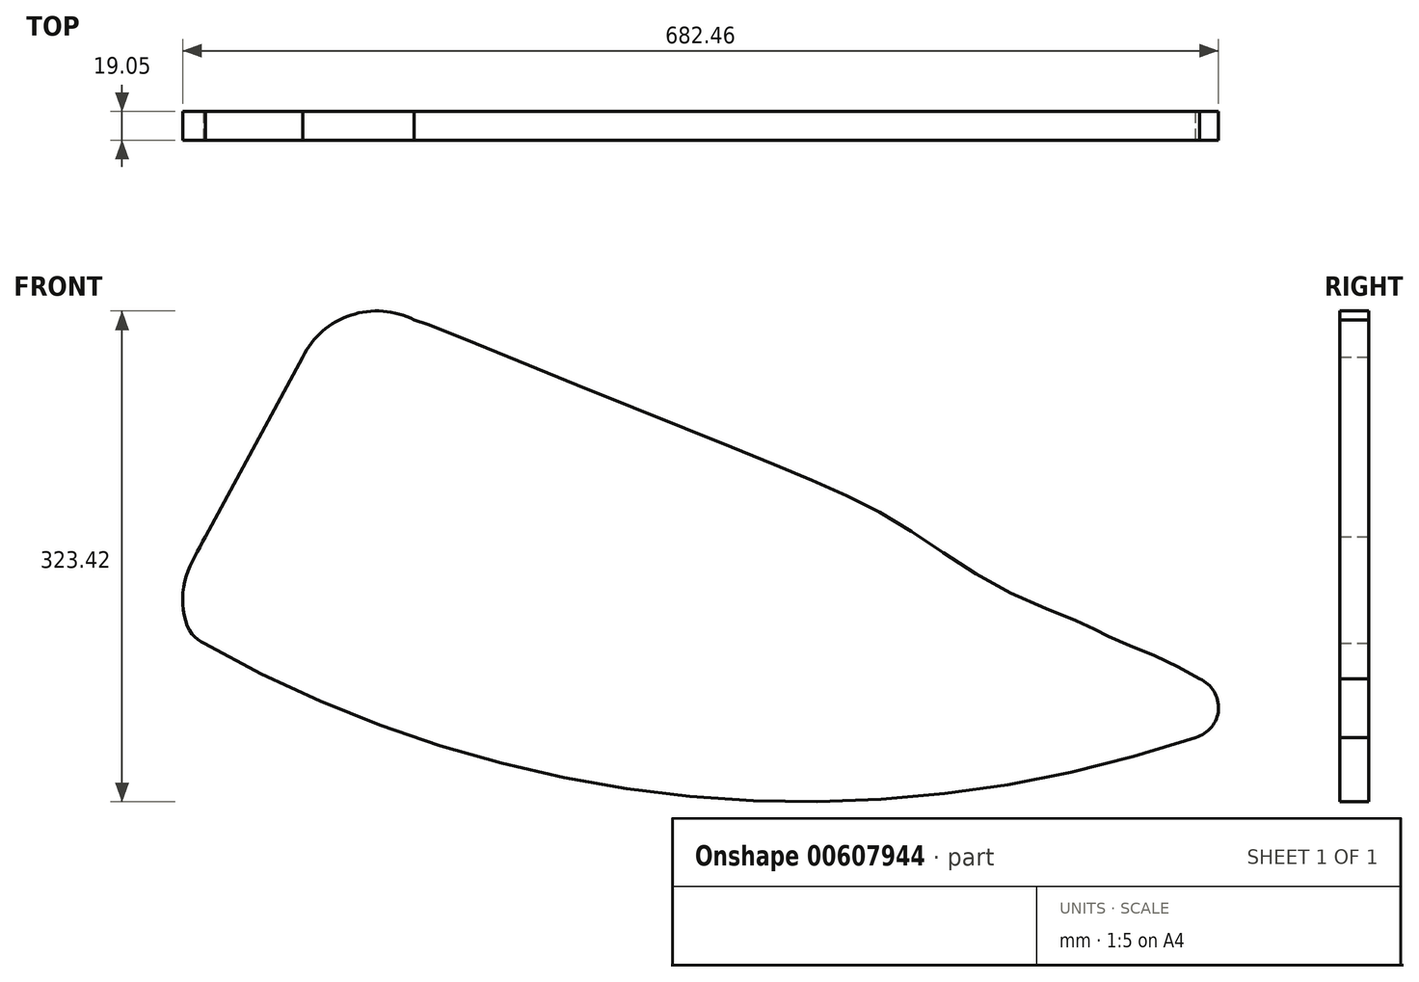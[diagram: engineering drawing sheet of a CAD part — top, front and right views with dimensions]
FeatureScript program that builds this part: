
annotation { "Feature Type Name" : "Feature", "Feature Type Description" : "" }
export const myFeature = defineFeature(function(context is Context, id is Id, definition is map)
    precondition{}
    {
        {
            var Q0;
            Q0=qCreatedBy(makeId("Front.planeOp"),FACE);
            var sketch = newSketch(context, id + "F0", { "sketchPlane" : qUnion([Q0])});
            skLineSegment(sketch, "E0", {"start": v(212, -92.36) * mm, "end": v(867.57, -172.12) * mm});
            skPoint(sketch, "E1.second.point", {"position": v(258.4, -166.58) * mm});
            skPoint(sketch, "E1.third.point", {"position": v(334.76, -150.1) * mm});
            skArc(sketch, "E2", {"start": v(257.5, -166.23) * mm, "mid": v(257.6, -166.27) * mm, "end": v(257.7, -166.3) * mm});
            skArc(sketch, "E3", {"start": v(212, -92.36) * mm, "mid": v(222.4, -136.9) * mm, "end": v(257.5, -166.23) * mm});
            skArc(sketch, "E4", {"start": v(413.86, -183.65) * mm, "mid": v(402.02, -162.17) * mm, "end": v(379.64, -152.15) * mm});
            skFitSpline(sketch, "E5", {"points": [v(257.7, -166.3) * mm, v(277.06, -161.4) * mm, v(306.96, -152.92) * mm, v(347.2, -150.1) * mm, v(379.64, -152.15) * mm], "startDerivative": vector(91.7, 21) * mm, "endDerivative": vector(120.47, -13) * mm});
            skFitSpline(sketch, "E6", {"points": [v(413.86, -183.65) * mm, v(412.03, -197.62) * mm, v(399.3, -208.1) * mm], "startDerivative": vector(5.3, -30.31) * mm, "endDerivative": vector(5.77, 3.53) * mm});
            skLineSegment(sketch, "E7", {"start": v(399.3, -208.1) * mm, "end": v(350.21, -235.12) * mm});
            skLineSegment(sketch, "E8", {"start": v(350.21, -235.12) * mm, "end": v(304.23, -269.25) * mm});
            skFitSpline(sketch, "E9", {"points": [v(198.6, -282.04) * mm, v(188.4, -308.65) * mm, v(187.64, -323.26) * mm, v(193.33, -340.27) * mm, v(197.89, -352.7) * mm, v(199.78, -357.87) * mm, v(199.1, -367.22) * mm, v(191.93, -383.75) * mm, v(181.7, -397.91) * mm, v(155.42, -431.43) * mm, v(96.73, -520) * mm, v(60.42, -582.5) * mm, v(26.9, -656.55) * mm], "startDerivative": vector(-151.16, -349.76) * mm, "endDerivative": vector(-240.56, -560.67) * mm});
            skFitSpline(sketch, "E10", {"points": [v(198.6, -282.04) * mm, v(224.24, -287.32) * mm, v(256.8, -287.13) * mm, v(304.23, -269.25) * mm], "startDerivative": vector(87.75, -20.82) * mm, "endDerivative": vector(123.62, 56.7) * mm});
            skPoint(sketch, "E11.second.point", {"position": v(986.17, -706.4) * mm});
            skPoint(sketch, "E11.third.point", {"position": v(696.86, 1694) * mm});
            skArc(sketch, "E12", {"start": v(26.9, -656.55) * mm, "mid": v(501.53, -778.1) * mm, "end": v(986.19, -706.4) * mm});
            skArc(sketch, "E13", {"start": v(1062.11, -709.33) * mm, "mid": v(1024.33, -703.2) * mm, "end": v(986.19, -706.4) * mm});
            skArc(sketch, "E14", {"start": v(1062.11, -709.33) * mm, "mid": v(1049.2, -671.33) * mm, "end": v(1017.89, -646.22) * mm});
            skFitSpline(sketch, "E15", {"points": [v(1017.89, -646.22) * mm, v(950.64, -624.3) * mm, v(867.47, -588.27) * mm, v(750.43, -525.1) * mm, v(692.28, -480.57) * mm, v(678.95, -454.88) * mm, v(674.6, -433.45) * mm], "startDerivative": vector(-386.65, 118.43) * mm, "endDerivative": vector(-20.4, 145.54) * mm});
            skLineSegment(sketch, "E16", {"start": v(674.6, -433.45) * mm, "end": v(580.77, -392.2) * mm});
            skFitSpline(sketch, "E17", {"points": [v(580.77, -392.2) * mm, v(541.24, -397.55) * mm, v(480.46, -385.66) * mm, v(421.84, -364.58) * mm, v(390.23, -348.1) * mm, v(380.5, -327.65) * mm, v(388.88, -304.15) * mm, v(405.1, -279.57) * mm, v(442.91, -253.9) * mm, v(531.07, -211.77) * mm, v(595.37, -198) * mm, v(725.3, -191) * mm, v(790.73, -196.17) * mm, v(850.7, -194.28) * mm, v(864.75, -189.7) * mm, v(867.57, -172.12) * mm], "startDerivative": vector(-611.1, -137.7) * mm, "endDerivative": vector(6.45, 510.82) * mm});
            skArc(sketch, "E18", {"start": v(185.8, -615.73) * mm, "mid": v(505.82, -716.5) * mm, "end": v(839.08, -677.71) * mm});
            skArc(sketch, "E19", {"start": v(839.08, -677.71) * mm, "mid": v(854.04, -659.38) * mm, "end": v(841.77, -639.15) * mm});
            skFitSpline(sketch, "E20", {"points": [v(841.77, -639.15) * mm, v(810.35, -623.1) * mm, v(780.37, -610.67) * mm, v(767.8, -603.91) * mm, v(711.73, -579.77) * mm, v(642.9, -536.33) * mm, v(572.78, -502.55) * mm, v(438.6, -448.24) * mm, v(324.82, -402.6) * mm, v(324.28, -402.6) * mm], "startDerivative": vector(-329.33, 181.66) * mm, "endDerivative": vector(-26.74, -9.02) * mm});
            skArc(sketch, "E21", {"start": v(324.28, -402.6) * mm, "mid": v(282.37, -399.44) * mm, "end": v(250.64, -427) * mm});
            skLineSegment(sketch, "E22", {"start": v(250.64, -427) * mm, "end": v(186.54, -545.3) * mm});
            skFitSpline(sketch, "E23", {"points": [v(186.54, -545.3) * mm, v(178.02, -561.74) * mm, v(172.38, -578.3) * mm, v(172.73, -597.68) * mm, v(178.72, -610.71) * mm, v(185.8, -615.73) * mm], "startDerivative": vector(-40.54, -79.02) * mm, "endDerivative": vector(49.66, -26.61) * mm});
            skSolve(sketch);
        }
        {
            var Q0;
            Q0 = qSketchRegion(id + "F0", true);
            extrude(context, id + "F1", {"entities" : qUnion([Q0]), "depth" : 19.05 * mm, "offsetDistance" : 25.4 * mm});
        }
    });
